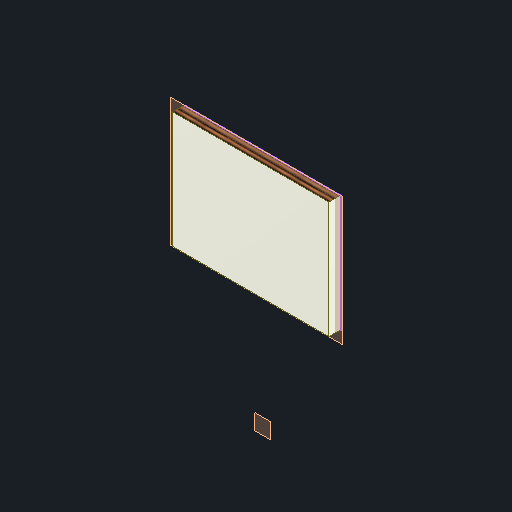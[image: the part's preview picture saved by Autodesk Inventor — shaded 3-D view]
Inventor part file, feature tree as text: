
AUTODESK INVENTOR PART (.ipt)
format: ipt  version: 2022 (Build 260153070, 153G)  size: 93,696 bytes
history: native  units: mm
features: other x3, sketch x1, extrude x1
ambient origin geometry x8: Origin, YZ Plane, XZ Plane, XY Plane, X Axis, Y Axis, Z Axis, Center Point
bodies: Body1 (feature_tree)
feature tree (5):
  other  "Твердое тело1"
  other  "РабПлоскость5"
  sketch  "Эскиз1"
  extrude  "Выдавливание1"  Depth=16.0mm TaperAngle=0.0deg
  other  "РабПлоскость6"
